# Revit family: Vents_VCUN
name_source: partatom
category: Оборудование
units: mm (PartAtom-declared; Revit-internal decimal feet)

## family parameters
Всегда вертикально = Да
Классификация = Нет
На основе рабочей плоскости = Нет
Общий = Нет
При загрузке вырезать с полостями = Нет
Размер круглого соединителя = Использовать диаметр
Тип детали = Нормальный
Точка принадлежности помещению = Нет

## types (31) — shared parameters
00_20_Виробник = Вентс
00_20_Назва = Відцентровий вентилятор в спіральному корпусі
Hd = 450 мм
URL = https://vents.ua
X2 = 12 мм
Изготовитель = Вентс
Класифікація навантаження = HVAC
Кількість фаз = 3
Матеріал зони обслуговуваня = <По категории>
Матеріал корпусу = Метал, пофарбований, синій, матовий RAL 5007
Напруга = 400 В
Температура повітря, що переміщається = 60°С
Частота = 50 Гц
zero-valued in all types: Отметка по умолчанию

## per-type parameters (varying)
- ВЦУН 500х229-11,0-4: 00_20_Тип=ВЦУН 500х229-11,0-4; B=860 мм; D=500 мм; F=48 мм; H=1115 мм; H1=390 мм; H2=341 мм; H3=534 мм; Hy=355 мм; L=761 мм; L1=401 мм; L2=353 мм; Ly=355 мм; R=250 мм; R1=464 мм; R2=450 мм; R3=340 мм; X1=483 мм; X3=250 мм; X4=365 мм; Y1=15 мм; Y2=330 мм; Y3=190 мм; Y4=531 мм; d=11 мм; f=24 мм; l=177 мм; r1=31 мм; r2=145 мм; Вага=107.00 кг; Висота=1115 мм; Двигатель=Двигатель : Двигатель_11 кВт; Довжина=824 мм; Діаметр=500 мм; Максимальний потік повітря=17250.0 м³/ч; Потужність=11000 Вт; Рама=Рама ВЦУН : Рама_500/11; Струм=24 А; Уголок рама=63 мм; Ширина=860 мм
- ВЦУН 140х74-0,37-2: 00_20_Тип=ВЦУН 140х74-0,37-2; B=242 мм; D=140 мм; F=30 мм; H=323 мм; H1=125 мм; H2=92 мм; H3=144 мм; Hy=100 мм; L=309 мм; L1=125 мм; L2=95 мм; Ly=100 мм; R=70 мм; R1=130 мм; R2=140 мм; R3=100 мм; X1=130 мм; X3=75 мм; X4=102 мм; Y1=15 мм; Y2=95 мм; Y3=57 мм; Y4=149 мм; d=8 мм; f=15 мм; l=48 мм; r1=9 мм; r2=39 мм; Вага=9.30 кг; Висота=323 мм; Двигатель=Двигатель : Двигатель_0.37 кВт; Довжина=344 мм; Діаметр=140 мм; Максимальний потік повітря=710.0 м³/ч; Потужність=370 Вт; Рама=Рама ВЦУН : Рама_140/0.37; Струм=1 А; Уголок рама=35 мм; Ширина=242 мм
- ВЦУН 160х74-0,55-4: 00_20_Тип=ВЦУН 160х74-0,55-4; B=277 мм; D=160 мм; F=30 мм; H=373 мм; H1=134 мм; H2=106 мм; H3=173 мм; Hy=112 мм; L=356 мм; L1=134 мм; L2=104 мм; Ly=112 мм; R=80 мм; R1=150 мм; R2=140 мм; R3=110 мм; X1=150 мм; X3=85 мм; X4=118 мм; Y1=15 мм; Y2=110 мм; Y3=64 мм; Y4=170 мм; d=8 мм; f=15 мм; l=52 мм; r1=10 мм; r2=42 мм; Вага=12.70 кг; Висота=373 мм; Двигатель=Двигатель : Двигатель_0.55 кВт; Довжина=391 мм; Діаметр=160 мм; Максимальний потік повітря=750.0 м³/ч; Потужність=550 Вт; Рама=Рама ВЦУН : Рама_160/0.55; Струм=2 А; Уголок рама=35 мм; Ширина=277 мм
- ВЦУН 160х74-0,75-2: 00_20_Тип=ВЦУН 160х74-0,75-2; B=277 мм; D=160 мм; F=30 мм; H=373 мм; H1=134 мм; H2=106 мм; H3=173 мм; Hy=112 мм; L=356 мм; L1=134 мм; L2=104 мм; Ly=112 мм; R=80 мм; R1=150 мм; R2=140 мм; R3=110 мм; X1=150 мм; X3=85 мм; X4=118 мм; Y1=15 мм; Y2=110 мм; Y3=64 мм; Y4=170 мм; d=8 мм; f=15 мм; l=52 мм; r1=10 мм; r2=42 мм; Вага=13.00 кг; Висота=373 мм; Двигатель=Двигатель : Двигатель_0.75 кВт; Довжина=391 мм; Діаметр=160 мм; Максимальний потік повітря=1540.0 м³/ч; Потужність=750 Вт; Рама=Рама ВЦУН : Рама_160/0.75; Струм=2 А; Уголок рама=35 мм; Ширина=277 мм
- ВЦУН 180х74-0,55-4: 00_20_Тип=ВЦУН 180х74-0,55-4; B=311 мм; D=180 мм; F=29 мм; H=414 мм; H1=143 мм; H2=120 мм; H3=193 мм; Hy=125 мм; L=365 мм; L1=143 мм; L2=114 мм; Ly=118 мм; R=90 мм; R1=170 мм; R2=160 мм; R3=120 мм; X1=170 мм; X3=85 мм; X4=132 мм; Y1=15 мм; Y2=130 мм; Y3=72 мм; Y4=192 мм; d=10 мм; f=15 мм; l=57 мм; r1=11 мм; r2=46 мм; Вага=13.50 кг; Висота=414 мм; Двигатель=Двигатель : Двигатель_0.55 кВт; Довжина=405 мм; Діаметр=180 мм; Максимальний потік повітря=1030.0 м³/ч; Потужність=550 Вт; Рама=Рама ВЦУН : Рама_180/0.55; Струм=2 А; Уголок рама=40 мм; Ширина=311 мм
- ВЦУН 180х74-1,1-2: 00_20_Тип=ВЦУН 180х74-0,55-4; B=345 мм; D=180 мм; F=29 мм; H=414 мм; H1=143 мм; H2=120 мм; H3=193 мм; Hy=125 мм; L=365 мм; L1=143 мм; L2=114 мм; Ly=118 мм; R=90 мм; R1=170 мм; R2=160 мм; R3=120 мм; X1=170 мм; X3=85 мм; X4=132 мм; Y1=15 мм; Y2=130 мм; Y3=72 мм; Y4=192 мм; d=10 мм; f=15 мм; l=57 мм; r1=11 мм; r2=46 мм; Вага=14.50 кг; Висота=414 мм; Двигатель=Двигатель : Двигатель_1.1 кВт/200; Довжина=405 мм; Діаметр=180 мм; Максимальний потік повітря=1950.0 м³/ч; Потужність=1100 Вт; Рама=Рама ВЦУН : Рама_180/1.1; Струм=3 А; Уголок рама=40 мм; Ширина=345 мм
- ВЦУН 200х93-0,55-4: 00_20_Тип=ВЦУН 200х93-0,55-4; B=345 мм; D=200 мм; F=31 мм; H=436 мм; H1=160 мм; H2=134 мм; H3=193 мм; Hy=125 мм; L=380 мм; L1=160 мм; L2=129 мм; Ly=118 мм; R=100 мм; R1=175 мм; R2=150 мм; R3=150 мм; X1=170 мм; X3=120 мм; X4=162 мм; Y1=15 мм; Y2=140 мм; Y3=79 мм; Y4=213 мм; d=10 мм; f=16 мм; l=65 мм; r1=13 мм; r2=52 мм; Вага=15.20 кг; Висота=436 мм; Двигатель=Двигатель : Двигатель_0.55 кВт; Довжина=420 мм; Діаметр=200 мм; Максимальний потік повітря=1615.0 м³/ч; Потужність=550 Вт; Рама=Рама ВЦУН : Рама_200/0.55; Струм=2 А; Уголок рама=40 мм; Ширина=345 мм
- ВЦУН 200х93-1,1-2: 00_20_Тип=ВЦУН 200х93-1,1-2; B=345 мм; D=200 мм; F=31 мм; H=436 мм; H1=160 мм; H2=134 мм; H3=193 мм; Hy=125 мм; L=380 мм; L1=160 мм; L2=129 мм; Ly=118 мм; R=100 мм; R1=175 мм; R2=150 мм; R3=150 мм; X1=170 мм; X3=120 мм; X4=162 мм; Y1=15 мм; Y2=140 мм; Y3=79 мм; Y4=213 мм; d=10 мм; f=16 мм; l=65 мм; r1=13 мм; r2=52 мм; Вага=16.20 кг; Висота=436 мм; Двигатель=Двигатель : Двигатель_1.1 кВт/200; Довжина=420 мм; Діаметр=200 мм; Максимальний потік повітря=1900.0 м³/ч; Потужність=1100 Вт; Рама=Рама ВЦУН : Рама_200/1.1; Струм=3 А; Уголок рама=40 мм; Ширина=345 мм
- ВЦУН 225х103-1,1-4: 00_20_Тип=ВЦУН 225х103-1,1-4; B=388 мм; D=225 мм; F=31 мм; H=507 мм; H1=178 мм; H2=151 мм; H3=232 мм; Hy=160 мм; L=432 мм; L1=172 мм; L2=141 мм; Ly=150 мм; R=113 мм; R1=200 мм; R2=180 мм; R3=150 мм; X1=170 мм; X3=120 мм; X4=204 мм; Y1=15 мм; Y2=140 мм; Y3=94 мм; Y4=245 мм; d=10 мм; f=16 мм; l=71 мм; r1=14 мм; r2=56 мм; Вага=21.20 кг; Висота=507 мм; Двигатель=Двигатель : Двигатель_1.1 кВт; Довжина=477 мм; Діаметр=225 мм; Максимальний потік повітря=2125.0 м³/ч; Потужність=1100 Вт; Рама=Рама ВЦУН : Рама_225/1.1; Струм=3 А; Уголок рама=45 мм; Ширина=388 мм
- ВЦУН 225х103-2,2-2: 00_20_Тип=ВЦУН 225х103-2,2-2; B=388 мм; D=225 мм; F=31 мм; H=507 мм; H1=178 мм; H2=151 мм; H3=232 мм; Hy=160 мм; L=432 мм; L1=172 мм; L2=141 мм; Ly=150 мм; R=113 мм; R1=200 мм; R2=180 мм; R3=150 мм; X1=170 мм; X3=120 мм; X4=204 мм; Y1=15 мм; Y2=140 мм; Y3=94 мм; Y4=245 мм; d=10 мм; f=16 мм; l=71 мм; r1=14 мм; r2=56 мм; Вага=24.20 кг; Висота=507 мм; Двигатель=Двигатель : Двигатель_2.2 кВт/225; Довжина=477 мм; Діаметр=225 мм; Максимальний потік повітря=3350.0 м³/ч; Потужність=2200 Вт; Рама=Рама ВЦУН : Рама_225/2.2; Струм=5 А; Уголок рама=45 мм; Ширина=388 мм
- ВЦУН 240х114-2,2-4: 00_20_Тип=ВЦУН 240х114-2,2-4; B=414 мм; D=240 мм; F=30 мм; H=568 мм; H1=186 мм; H2=161 мм; H3=282 мм; Hy=170 мм; L=461 мм; L1=186 мм; L2=156 мм; Ly=160 мм; R=120 мм; R1=210 мм; R2=210 мм; R3=160 мм; X1=200 мм; X3=130 мм; X4=200 мм; Y1=15 мм; Y2=160 мм; Y3=95 мм; Y4=256 мм; d=10 мм; f=15 мм; l=78 мм; r1=15 мм; r2=63 мм; Вага=30.50 кг; Висота=568 мм; Двигатель=Двигатель : Двигатель_2.2 кВт/280; Довжина=506 мм; Діаметр=240 мм; Максимальний потік повітря=2930.0 м³/ч; Потужність=2200 Вт; Рама=Рама ВЦУН : Рама_240/2.2; Струм=5 А; Уголок рама=45 мм; Ширина=414 мм
- ВЦУН 240х114-3,0-2: 00_20_Тип=ВЦУН 240х114-3,0-2; B=414 мм; D=240 мм; F=30 мм; H=568 мм; H1=186 мм; H2=161 мм; H3=282 мм; Hy=170 мм; L=461 мм; L1=186 мм; L2=156 мм; Ly=160 мм; R=120 мм; R1=210 мм; R2=210 мм; R3=160 мм; X1=200 мм; X3=130 мм; X4=200 мм; Y1=15 мм; Y2=160 мм; Y3=95 мм; Y4=256 мм; d=10 мм; f=15 мм; l=78 мм; r1=15 мм; r2=63 мм; Вага=31.40 кг; Висота=568 мм; Двигатель=Двигатель : Двигатель_3 кВт/240; Довжина=506 мм; Діаметр=240 мм; Максимальний потік повітря=4350.0 м³/ч; Потужність=3000 Вт; Рама=Рама ВЦУН : Рама_240/3; Струм=6 А; Уголок рама=45 мм; Ширина=414 мм
- ВЦУН 250х127-1,5-6: 00_20_Тип=ВЦУН 250х127-1,5-6; B=431 мм; D=250 мм; F=36 мм; H=594 мм; H1=202 мм; H2=168 мм; H3=292 мм; Hy=170 мм; L=473 мм; L1=202 мм; L2=166 мм; Ly=170 мм; R=125 мм; R1=210 мм; R2=210 мм; R3=165 мм; X1=200 мм; X3=130 мм; X4=214 мм; Y1=15 мм; Y2=160 мм; Y3=98 мм; Y4=266 мм; d=10 мм; f=18 мм; l=83 мм; r1=16 мм; r2=67 мм; Вага=33.00 кг; Висота=594 мм; Двигатель=Двигатель : Двигатель_1.5 кВт/280; Довжина=523 мм; Діаметр=250 мм; Максимальний потік повітря=2415.0 м³/ч; Потужність=1500 Вт; Рама=Рама ВЦУН : Рама_250/1.5; Струм=4 А; Уголок рама=50 мм; Ширина=431 мм
- ВЦУН 250х127-2,2-4: 00_20_Тип=ВЦУН 250х127-2,2-4; B=431 мм; D=250 мм; F=36 мм; H=594 мм; H1=202 мм; H2=168 мм; H3=292 мм; Hy=170 мм; L=473 мм; L1=202 мм; L2=166 мм; Ly=170 мм; R=125 мм; R1=210 мм; R2=210 мм; R3=165 мм; X1=200 мм; X3=130 мм; X4=214 мм; Y1=15 мм; Y2=160 мм; Y3=98 мм; Y4=266 мм; d=10 мм; f=18 мм; l=83 мм; r1=16 мм; r2=67 мм; Вага=32.20 кг; Висота=594 мм; Двигатель=Двигатель : Двигатель_2.2 кВт/280; Довжина=523 мм; Діаметр=250 мм; Максимальний потік повітря=3720.0 м³/ч; Потужність=2200 Вт; Рама=Рама ВЦУН : Рама_250/2.2; Струм=5 А; Уголок рама=50 мм; Ширина=431 мм
- ВЦУН 250х127-5,5-2: 00_20_Тип=ВЦУН 250х127-5,5-2; B=431 мм; D=250 мм; F=36 мм; H=614 мм; H1=202 мм; H2=168 мм; H3=312 мм; Hy=170 мм; L=517 мм; L1=202 мм; L2=166 мм; Ly=170 мм; R=125 мм; R1=210 мм; R2=210 мм; R3=165 мм; X1=200 мм; X3=130 мм; X4=214 мм; Y1=15 мм; Y2=160 мм; Y3=98 мм; Y4=266 мм; d=10 мм; f=18 мм; l=83 мм; r1=16 мм; r2=67 мм; Вага=40.00 кг; Висота=614 мм; Двигатель=Двигатель : Двигатель_5.5 кВт/280; Довжина=567 мм; Діаметр=250 мм; Максимальний потік повітря=4820.0 м³/ч; Потужність=5500 Вт; Рама=Рама ВЦУН : Рама_250/5.5; Струм=11 А; Уголок рама=50 мм; Ширина=431 мм
- ВЦУН 280х127-1,5-6: 00_20_Тип=ВЦУН 280х127-1,5-6; B=483 мм; D=280 мм; F=35 мм; H=626 мм; H1=225 мм; H2=189 мм; H3=292 мм; Hy=190 мм; L=503 мм; L1=231 мм; L2=196 мм; Ly=200 мм; R=140 мм; R1=260 мм; R2=250 мм; R3=180 мм; X1=250 мм; X3=130 мм; X4=222 мм; Y1=15 мм; Y2=180 мм; Y3=110 мм; Y4=299 мм; d=10 мм; f=18 мм; l=98 мм; r1=18 мм; r2=81 мм; Вага=35.10 кг; Висота=626 мм; Двигатель=Двигатель : Двигатель_1.5 кВт/280; Довжина=553 мм; Діаметр=280 мм; Максимальний потік повітря=3450.0 м³/ч; Потужність=1500 Вт; Рама=Рама ВЦУН : Рама_280/1.5; Струм=4 А; Уголок рама=50 мм; Ширина=483 мм
- ВЦУН 280х127-2,2-4: 00_20_Тип=ВЦУН 280х127-2,2-4; B=483 мм; D=280 мм; F=35 мм; H=626 мм; H1=225 мм; H2=189 мм; H3=292 мм; Hy=190 мм; L=503 мм; L1=231 мм; L2=196 мм; Ly=200 мм; R=140 мм; R1=260 мм; R2=250 мм; R3=180 мм; X1=250 мм; X3=130 мм; X4=222 мм; Y1=15 мм; Y2=180 мм; Y3=110 мм; Y4=299 мм; d=10 мм; f=18 мм; l=98 мм; r1=18 мм; r2=81 мм; Вага=34.20 кг; Висота=626 мм; Двигатель=Двигатель : Двигатель_2.2 кВт/280; Довжина=553 мм; Діаметр=280 мм; Максимальний потік повітря=4395.0 м³/ч; Потужність=2200 Вт; Рама=Рама ВЦУН : Рама_280/2.2; Струм=5 А; Уголок рама=50 мм; Ширина=483 мм
- ВЦУН 280х127-5,5-2: 00_20_Тип=ВЦУН 280х127-5,5-2; B=483 мм; D=280 мм; F=35 мм; H=646 мм; H1=225 мм; H2=189 мм; H3=312 мм; Hy=190 мм; L=545 мм; L1=231 мм; L2=196 мм; Ly=200 мм; R=140 мм; R1=260 мм; R2=250 мм; R3=180 мм; X1=250 мм; X3=130 мм; X4=222 мм; Y1=15 мм; Y2=180 мм; Y3=110 мм; Y4=299 мм; d=10 мм; f=18 мм; l=98 мм; r1=18 мм; r2=81 мм; Вага=42.40 кг; Висота=646 мм; Двигатель=Двигатель : Двигатель_5.5 кВт/280; Довжина=595 мм; Діаметр=280 мм; Максимальний потік повітря=6330.0 м³/ч; Потужність=5500 Вт; Рама=Рама ВЦУН : Рама_280/5.5; Струм=11 А; Уголок рама=50 мм; Ширина=483 мм
- ВЦУН 315х143-2,2-6: 00_20_Тип=ВЦУН 315х143-2,2-6; B=543 мм; D=315 мм; F=39 мм; H=731 мм; H1=250 мм; H2=213 мм; H3=353 мм; Hy=224 мм; L=568 мм; L1=255 мм; L2=216 мм; Ly=224 мм; R=158 мм; R1=300 мм; R2=240 мм; R3=200 мм; X1=260 мм; X3=150 мм; X4=273 мм; Y1=15 мм; Y2=200 мм; Y3=126 мм; Y4=339 мм; d=10 мм; f=20 мм; l=108 мм; r1=20 мм; r2=88 мм; Вага=46.80 кг; Висота=731 мм; Двигатель=Двигатель : Двигатель_2.2 кВт; Довжина=618 мм; Діаметр=315 мм; Максимальний потік повітря=4375.0 м³/ч; Потужність=2200 Вт; Рама=Рама ВЦУН : Рама_315/2.2; Струм=6 А; Уголок рама=50 мм; Ширина=543 мм
- ВЦУН 315х143-4,0-4: 00_20_Тип=ВЦУН 315х143-4,0-4; B=543 мм; D=315 мм; F=39 мм; H=731 мм; H1=250 мм; H2=213 мм; H3=353 мм; Hy=224 мм; L=568 мм; L1=255 мм; L2=216 мм; Ly=224 мм; R=158 мм; R1=300 мм; R2=240 мм; R3=200 мм; X1=260 мм; X3=150 мм; X4=273 мм; Y1=15 мм; Y2=200 мм; Y3=126 мм; Y4=339 мм; d=10 мм; f=20 мм; l=108 мм; r1=20 мм; r2=88 мм; Вага=49.80 кг; Висота=731 мм; Двигатель=Двигатель : Двигатель_4 кВт/355; Довжина=618 мм; Діаметр=315 мм; Максимальний потік повітря=6530.0 м³/ч; Потужність=4000 Вт; Рама=Рама ВЦУН : Рама_315/4; Струм=9 А; Уголок рама=50 мм; Ширина=543 мм
- ВЦУН 355х143-2,2-6: 00_20_Тип=ВЦУН 355х143-2,2-6; B=611 мм; D=355 мм; F=41 мм; H=817 мм; H1=275 мм; H2=241 мм; H3=403 мм; Hy=250 мм; L=566 мм; L1=255 мм; L2=214 мм; Ly=224 мм; R=178 мм; R1=300 мм; R2=280 мм; R3=225 мм; X1=280 мм; X3=180 мм; X4=317 мм; Y1=0 мм; Y2=230 мм; Y3=132 мм; Y4=373 мм; d=10 мм; f=21 мм; l=107 мм; r1=22 мм; r2=85 мм; Вага=49.00 кг; Висота=817 мм; Двигатель=Двигатель : Двигатель_2.2 кВт; Довжина=616 мм; Діаметр=355 мм; Максимальний потік повітря=5090.0 м³/ч; Потужність=2200 Вт; Рама=Рама ВЦУН : Рама_355/2.2; Струм=6 А; Уголок рама=50 мм; Ширина=611 мм
- ВЦУН 355х143-4,0-4: 00_20_Тип=ВЦУН 355х143-4,0-4; B=611 мм; D=355 мм; F=41 мм; H=817 мм; H1=275 мм; H2=241 мм; H3=403 мм; Hy=250 мм; L=566 мм; L1=255 мм; L2=214 мм; Ly=224 мм; R=178 мм; R1=300 мм; R2=280 мм; R3=225 мм; X1=280 мм; X3=180 мм; X4=317 мм; Y1=0 мм; Y2=230 мм; Y3=132 мм; Y4=373 мм; d=10 мм; f=21 мм; l=107 мм; r1=22 мм; r2=85 мм; Вага=51.00 кг; Висота=817 мм; Двигатель=Двигатель : Двигатель_4 кВт/355; Довжина=616 мм; Діаметр=355 мм; Максимальний потік повітря=8150.0 м³/ч; Потужність=4000 Вт; Рама=Рама ВЦУН : Рама_355/4; Струм=9 А; Уголок рама=50 мм; Ширина=611 мм
- ВЦУН 400х183-1,5-8: 00_20_Тип=ВЦУН 400х183-1,5-8; B=689 мм; D=400 мм; F=42 мм; H=870 мм; H1=310 мм; H2=272 мм; H3=403 мм; Hy=280 мм; L=619 мм; L1=310 мм; L2=268 мм; Ly=280 мм; R=200 мм; R1=340 мм; R2=320 мм; R3=260 мм; X1=320 мм; X3=210 мм; X4=343 мм; Y1=60 мм; Y2=280 мм; Y3=126 мм; Y4=398 мм; d=10 мм; f=21 мм; l=134 мм; r1=25 мм; r2=109 мм; Вага=57.10 кг; Висота=870 мм; Двигатель=Двигатель : Двигатель_1.5 кВт; Довжина=669 мм; Діаметр=400 мм; Максимальний потік повітря=6545.0 м³/ч; Потужність=1500 Вт; Рама=Рама ВЦУН : Рама_400/1.5; Струм=4 А; Уголок рама=50 мм; Ширина=689 мм
- ВЦУН 400х183-2,2-6: 00_20_Тип=ВЦУН 400х183-2,2-6; B=689 мм; D=400 мм; F=42 мм; H=870 мм; H1=310 мм; H2=272 мм; H3=403 мм; Hy=280 мм; L=619 мм; L1=310 мм; L2=268 мм; Ly=280 мм; R=200 мм; R1=340 мм; R2=320 мм; R3=260 мм; X1=320 мм; X3=210 мм; X4=343 мм; Y1=60 мм; Y2=280 мм; Y3=126 мм; Y4=398 мм; d=10 мм; f=21 мм; l=134 мм; r1=25 мм; r2=109 мм; Вага=54.10 кг; Висота=870 мм; Двигатель=Двигатель : Двигатель_2.2 кВт; Довжина=669 мм; Діаметр=400 мм; Максимальний потік повітря=8100.0 м³/ч; Потужність=2200 Вт; Рама=Рама ВЦУН : Рама_400/2.2; Струм=6 А; Уголок рама=50 мм; Ширина=689 мм
- ВЦУН 400х183-5,5-4: 00_20_Тип=ВЦУН 400х183-5,5-4; B=689 мм; D=400 мм; F=41 мм; H=882 мм; H1=310 мм; H2=272 мм; H3=414 мм; Hy=280 мм; L=662 мм; L1=330 мм; L2=289 мм; Ly=300 мм; R=200 мм; R1=360 мм; R2=320 мм; R3=275 мм; X1=320 мм; X3=210 мм; X4=341 мм; Y1=60 мм; Y2=280 мм; Y3=155 мм; Y4=427 мм; d=10 мм; f=21 мм; l=145 мм; r1=25 мм; r2=120 мм; Вага=69.50 кг; Висота=882 мм; Двигатель=Двигатель : Двигатель_5.5 кВт/400; Довжина=712 мм; Діаметр=400 мм; Максимальний потік повітря=10175.0 м³/ч; Потужність=5500 Вт; Рама=Рама ВЦУН : Рама_400/5.5; Струм=11 А; Уголок рама=50 мм; Ширина=689 мм
- ВЦУН 450х203-3,0-8: 00_20_Тип=ВЦУН 450х203-3,0-8; B=774 мм; D=450 мм; F=37 мм; H=985 мм; H1=345 мм; H2=306 мм; H3=464 мм; Hy=315 мм; L=690 мм; L1=352 мм; L2=315 мм; Ly=315 мм; R=225 мм; R1=400 мм; R2=360 мм; R3=300 мм; X1=350 мм; X3=240 мм; X4=392 мм; Y1=60 мм; Y2=310 мм; Y3=178 мм; Y4=484 мм; d=10 мм; f=19 мм; l=158 мм; r1=28 мм; r2=129 мм; Вага=77.80 кг; Висота=985 мм; Двигатель=Двигатель : Двигатель_3 кВт; Довжина=753 мм; Діаметр=450 мм; Максимальний потік повітря=10230.0 м³/ч; Потужність=3000 Вт; Рама=Рама ВЦУН : Рама_450/3; Струм=8 А; Уголок рама=63 мм; Ширина=774 мм
- ВЦУН 450х203-4,0-6: 00_20_Тип=ВЦУН 450х203-4,0-6; B=774 мм; D=450 мм; F=37 мм; H=985 мм; H1=345 мм; H2=306 мм; H3=464 мм; Hy=315 мм; L=690 мм; L1=352 мм; L2=315 мм; Ly=315 мм; R=225 мм; R1=400 мм; R2=360 мм; R3=300 мм; X1=350 мм; X3=240 мм; X4=392 мм; Y1=60 мм; Y2=310 мм; Y3=178 мм; Y4=484 мм; d=10 мм; f=19 мм; l=158 мм; r1=28 мм; r2=129 мм; Вага=76.50 кг; Висота=985 мм; Двигатель=Двигатель : Двигатель_4 кВт; Довжина=753 мм; Діаметр=450 мм; Максимальний потік повітря=11150.0 м³/ч; Потужність=4000 Вт; Рама=Рама ВЦУН : Рама_450/4; Струм=9 А; Уголок рама=63 мм; Ширина=774 мм
- ВЦУН 450х203-11,0-4: 00_20_Тип=ВЦУН 450х203-11,0-4; B=774 мм; D=450 мм; F=37 мм; H=1005 мм; H1=345 мм; H2=306 мм; H3=484 мм; Hy=315 мм; L=722 мм; L1=352 мм; L2=315 мм; Ly=315 мм; R=225 мм; R1=400 мм; R2=360 мм; R3=300 мм; X1=350 мм; X3=240 мм; X4=392 мм; Y1=60 мм; Y2=310 мм; Y3=178 мм; Y4=484 мм; d=10 мм; f=19 мм; l=158 мм; r1=28 мм; r2=129 мм; Вага=105.00 кг; Висота=1005 мм; Двигатель=Двигатель : Двигатель_11 кВт; Довжина=785 мм; Діаметр=450 мм; Максимальний потік повітря=19000.0 м³/ч; Потужність=11000 Вт; Рама=Рама ВЦУН : Рама_450/11; Струм=24 А; Уголок рама=63 мм; Ширина=774 мм
- ВЦУН 500х229-5,5-8: 00_20_Тип=ВЦУН 500х229-5,5-8; B=860 мм; D=500 мм; F=48 мм; H=1115 мм; H1=390 мм; H2=341 мм; H3=534 мм; Hy=355 мм; L=761 мм; L1=401 мм; L2=353 мм; Ly=355 мм; R=250 мм; R1=464 мм; R2=450 мм; R3=340 мм; X1=483 мм; X3=250 мм; X4=365 мм; Y1=15 мм; Y2=330 мм; Y3=190 мм; Y4=531 мм; d=11 мм; f=24 мм; l=177 мм; r1=31 мм; r2=145 мм; Вага=85.00 кг; Висота=1115 мм; Двигатель=Двигатель : Двигатель_5.5 кВт; Довжина=824 мм; Діаметр=500 мм; Максимальний потік повітря=11550.0 м³/ч; Потужність=5500 Вт; Рама=Рама ВЦУН : Рама_500/5.5; Струм=15 А; Уголок рама=63 мм; Ширина=860 мм
- ВЦУН 500х229-7,5-6: 00_20_Тип=ВЦУН 500х229-7,5-6; B=860 мм; D=500 мм; F=48 мм; H=1115 мм; H1=390 мм; H2=341 мм; H3=534 мм; Hy=355 мм; L=761 мм; L1=401 мм; L2=353 мм; Ly=355 мм; R=250 мм; R1=464 мм; R2=450 мм; R3=340 мм; X1=483 мм; X3=250 мм; X4=365 мм; Y1=15 мм; Y2=330 мм; Y3=190 мм; Y4=531 мм; d=11 мм; f=24 мм; l=177 мм; r1=31 мм; r2=145 мм; Вага=86.00 кг; Висота=1115 мм; Двигатель=Двигатель : Двигатель_7.5 кВт; Довжина=824 мм; Діаметр=500 мм; Максимальний потік повітря=14960.0 м³/ч; Потужність=7500 Вт; Рама=Рама ВЦУН : Рама_500/7.5; Струм=17 А; Уголок рама=63 мм; Ширина=860 мм
- ВЦУН 140х74-0,25-4: 00_20_Тип=ВЦУН 140х74-0,25-4; B=242 мм; D=140 мм; F=30 мм; H=323 мм; H1=125 мм; H2=92 мм; H3=144 мм; Hy=100 мм; L=309 мм; L1=125 мм; L2=95 мм; Ly=100 мм; R=70 мм; R1=130 мм; R2=140 мм; R3=100 мм; X1=130 мм; X3=75 мм; X4=102 мм; Y1=15 мм; Y2=95 мм; Y3=57 мм; Y4=149 мм; d=8 мм; f=15 мм; l=48 мм; r1=9 мм; r2=39 мм; Вага=9.30 кг; Висота=323 мм; Двигатель=Двигатель : Двигатель_0.25 кВт; Довжина=344 мм; Діаметр=140 мм; Максимальний потік повітря=450.0 м³/ч; Потужність=250 Вт; Рама=Рама ВЦУН : Рама_140/0.25; Струм=1 А; Уголок рама=35 мм; Ширина=242 мм
